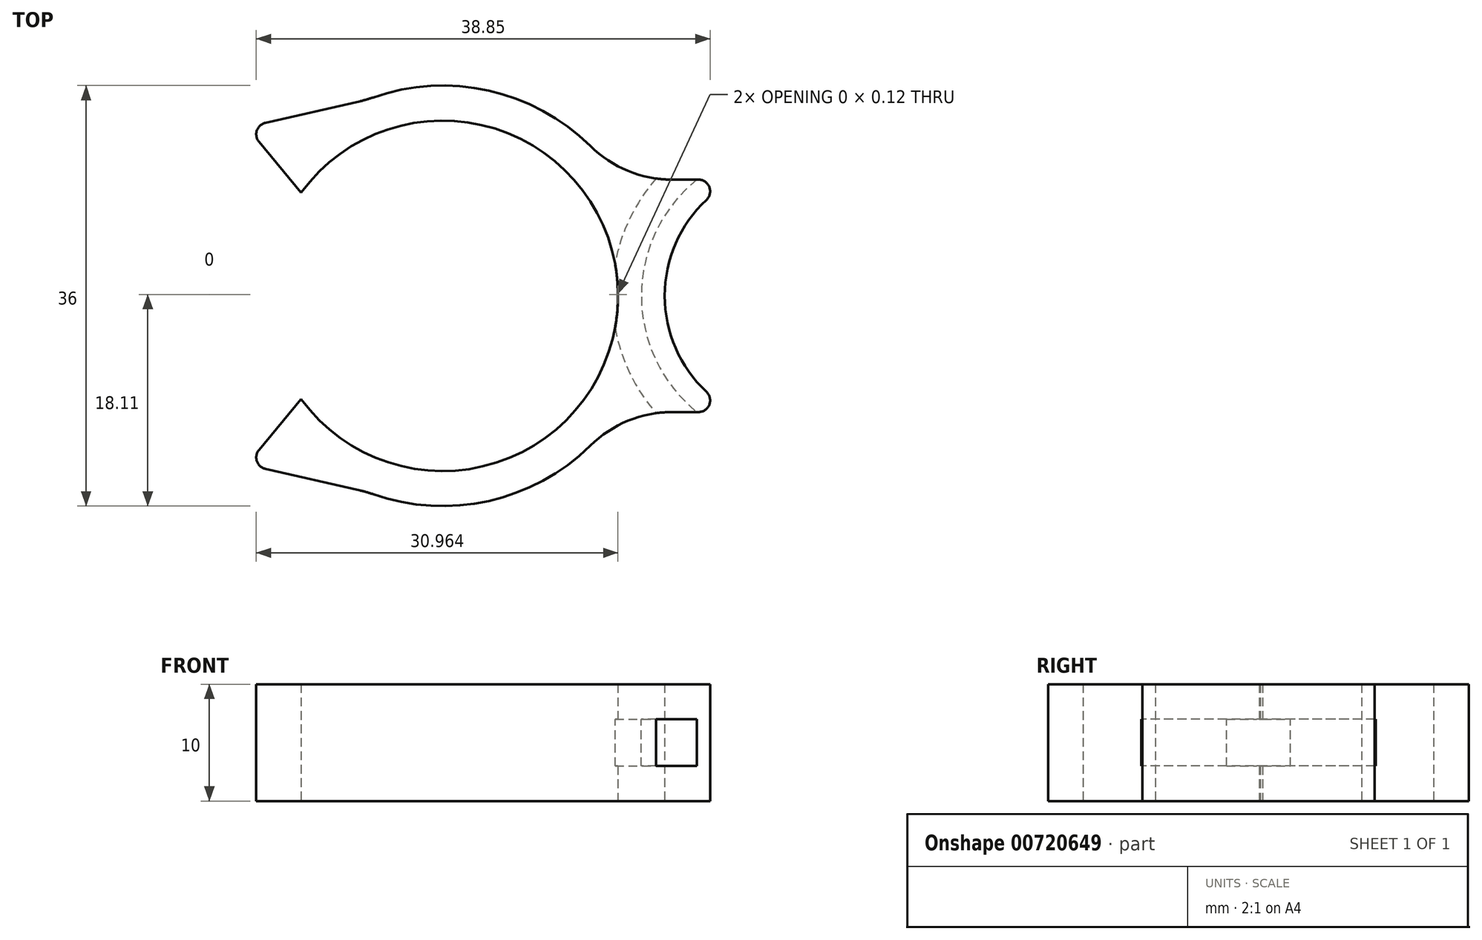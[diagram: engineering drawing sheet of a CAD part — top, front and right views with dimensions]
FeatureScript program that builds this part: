
annotation { "Feature Type Name" : "Feature", "Feature Type Description" : "" }
export const myFeature = defineFeature(function(context is Context, id is Id, definition is map)
    precondition{}
    {
        {
            var Q0;
            Q0=qCreatedBy(makeId("Top.planeOp"),FACE);
            var sketch = newSketch(context, id + "F0", { "sketchPlane" : qUnion([Q0])});
            skArc(sketch, "E0", {"start": v(-28.92, -8.84) * mm, "mid": v(-1.8, 0) * mm, "end": v(-28.92, 8.84) * mm});
            skArc(sketch, "E1", {"start": v(8.2, 9.95) * mm, "mid": v(2.2, 0) * mm, "end": v(8.2, -9.95) * mm});
            skArc(sketch, "E2", {"start": v(-23.25, -16.8) * mm, "mid": v(-11.32, -17.15) * mm, "end": v(-1.8, -9.95) * mm});
            skLineSegment(sketch, "E3", {"start": v(-16.8, 0) * mm, "end": v(13.45, 0) * mm, "construction": true});
            skPoint(sketch, "E4", {"position": v(-1.67, 0) * mm});
            skLineSegment(sketch, "E5.trimOffspring", {"start": v(-1.8, 0.05) * mm, "end": v(-1.8, 0.37) * mm});
            skLineSegment(sketch, "E6.bottom", {"start": v(8.2, 9.95) * mm, "end": v(-1.8, 9.95) * mm});
            skLineSegment(sketch, "E6.top", {"start": v(8.2, -9.95) * mm, "end": v(-1.8, -9.95) * mm});
            skLineSegment(sketch, "E6.right", {"start": v(-1.8, 0.17) * mm, "end": v(-1.8, 0.05) * mm});
            skLineSegment(sketch, "E7.trimOffspring", {"start": v(-1.8, 0.17) * mm, "end": v(-1.8, -0.16) * mm});
            skArc(sketch, "E8.trimOffspring", {"start": v(-1.8, 9.95) * mm, "mid": v(-11.32, 17.15) * mm, "end": v(-23.25, 16.8) * mm});
            skLineSegment(sketch, "E9", {"start": v(-28.92, 8.84) * mm, "end": v(-33.56, 14.45) * mm});
            skLineSegment(sketch, "E10", {"start": v(-33.56, 14.45) * mm, "end": v(-23.25, 16.8) * mm});
            skLineSegment(sketch, "E11.MirrorCS", {"start": v(-28.92, -8.84) * mm, "end": v(-33.56, -14.45) * mm});
            skLineSegment(sketch, "E12.MirrorCS", {"start": v(-33.56, -14.45) * mm, "end": v(-23.25, -16.8) * mm});
            skLineSegment(sketch, "E13", {"start": v(-9.06, 0) * mm, "end": v(-9.06, 9.95) * mm, "construction": true});
            skLineSegment(sketch, "E14", {"start": v(-9.06, 0) * mm, "end": v(-9.06, -9.95) * mm, "construction": true});
            skSolve(sketch);
        }
        {
            var Q0;
            Q0 = qSketchRegion(id + "F0", true);
            extrude(context, id + "F1", {"entities" : qUnion([Q0]), "depth" : 10 * mm, "offsetDistance" : 25 * mm});
        }
        {
            var Q0;
            Q0=makeQuery(id+"F1.opExtrude","SWEPT_EDGE",EDGE,{"disambiguationData":[OSD([sQuery(id+"F0.wireOp",EDGE,"IWztPc0H-4Czz-cEDn-FhKq-w9oCYmKX9AF6"),sQuery(id+"F0.wireOp",EDGE,"92DBHX5X-K6kR-Upr4-bK9H-dtZGLeEnyNnV")])]});
            var Q1;
            Q1=makeQuery(id+"F1.opExtrude","SWEPT_EDGE",EDGE,{"disambiguationData":[OSD([sQuery(id+"F0.wireOp",EDGE,"IWztPc0H-4Czz-cEDn-FhKq-w9oCYmKX9AF6"),sQuery(id+"F0.wireOp",EDGE,"024c119b-de07-41a7-b339-62df15f0e614.trimOffspring")])]});
            var Q2;
            Q2=makeQuery(id+"F1.opExtrude","SWEPT_EDGE",EDGE,{"disambiguationData":[OSD([sQuery(id+"F0.wireOp",EDGE,"3e003569-1aac-4e3d-9f3d-77501b08c2a10.MirrorCS"),sQuery(id+"F0.wireOp",EDGE,"be3c4033-0644-41de-af03-7eb39c3d72080.MirrorCS")])]});
            var Q3;
            Q3=makeQuery(id+"F1.opExtrude","SWEPT_EDGE",EDGE,{"disambiguationData":[OSD([sQuery(id+"F0.wireOp",EDGE,"MHDpRclH-q2Dj-4ouE-9ryf-v0UQ6AgA5fog"),sQuery(id+"F0.wireOp",EDGE,"Bm5BC6q6-ifkZ-6Eal-UUqP-6c5QV21PyJyv")])]});
            var Q4;
            Q4=makeQuery(id+"F1.opExtrude","SWEPT_EDGE",EDGE,{"disambiguationData":[OSD([sQuery(id+"F0.wireOp",EDGE,"E11.MirrorCS"),sQuery(id+"F0.wireOp",EDGE,"E12.MirrorCS")])]});
            var Q5;
            Q5=makeQuery(id+"F1.opExtrude","SWEPT_EDGE",EDGE,{"disambiguationData":[OSD([sQuery(id+"F0.wireOp",EDGE,"E9"),sQuery(id+"F0.wireOp",EDGE,"E10")])]});
            fillet(context, id + "F2", {"entities" : qUnion([Q0, Q1, Q2, Q3, Q4, Q5]), "tangentPropagation" : true, "radius" : 1 * mm, "defaultsChanged" : false, "vertexSettings" : [], "allowEdgeOverflow" : false});
        }
        {
            var Q0;
            Q0=makeQuery(id+"F1.opExtrude","SWEPT_EDGE",EDGE,{"disambiguationData":[OSD([sQuery(id+"F0.wireOp",EDGE,"E6.bottom"),sQuery(id+"F0.wireOp",EDGE,"E8.trimOffspring")])]});
            var Q1;
            Q1=makeQuery(id+"F1.opExtrude","SWEPT_EDGE",EDGE,{"disambiguationData":[OSD([sQuery(id+"F0.wireOp",EDGE,"E2"),sQuery(id+"F0.wireOp",EDGE,"E6.top")])]});
            var Q2;
            Q2=makeQuery(id+"F1.opExtrude","SWEPT_EDGE",EDGE,{"disambiguationData":[OSD([sQuery(id+"F0.wireOp",EDGE,"E8.trimOffspring"),sQuery(id+"F0.wireOp",EDGE,"E10")])]});
            var Q3;
            Q3=makeQuery(id+"F1.opExtrude","SWEPT_EDGE",EDGE,{"disambiguationData":[OSD([sQuery(id+"F0.wireOp",EDGE,"E2"),sQuery(id+"F0.wireOp",EDGE,"E12.MirrorCS")])]});
            fillet(context, id + "F3", {"entities" : qUnion([Q0, Q1, Q2, Q3]), "tangentPropagation" : true, "radius" : 10 * mm, "defaultsChanged" : false, "vertexSettings" : [], "allowEdgeOverflow" : false});
        }
        {
            var Q0;
            Q0=makeQuery(id+"F1.opExtrude","CAP_FACE",FACE,{"disambiguationData":[OSD([sQuery(id+"F0.wireOp",EDGE,"E0"),sQuery(id+"F0.wireOp",EDGE,"E1"),sQuery(id+"F0.wireOp",EDGE,"E2"),sQuery(id+"F0.wireOp",EDGE,"MHDpRclH-q2Dj-4ouE-9ryf-v0UQ6AgA5fog"),sQuery(id+"F0.wireOp",EDGE,"78308c44-5025-46c9-aef0-875acc5395fe.trimOffspring"),sQuery(id+"F0.wireOp",EDGE,"E6.bottom"),sQuery(id+"F0.wireOp",EDGE,"E6.top"),sQuery(id+"F0.wireOp",EDGE,"E8.trimOffspring")])],"isStart":false});
            cPlane(context, id + "F4", {"entities" : qUnion([Q0]), "cplaneType" : CPlaneType.OFFSET, "offset" : 3 * mm, "oppositeDirection" : true, "width" : 150 * mm, "height" : 150 * mm});
        }
        {
            var Q0;
            Q0=qCreatedBy(id+"F4.planeOp",FACE);
            var sketch = newSketch(context, id + "F5", { "sketchPlane" : qUnion([Q0])});
            skArc(sketch, "E15", {"start": v(7.94, 11.74) * mm, "mid": v(0.34, -1.85) * mm, "end": v(11.53, -12.7) * mm});
            skArc(sketch, "E16", {"start": v(3.2, 11.74) * mm, "mid": v(-2.27, -0.8) * mm, "end": v(4.48, -12.7) * mm});
            skLineSegment(sketch, "E17", {"start": v(3.2, 11.74) * mm, "end": v(7.94, 11.74) * mm});
            skLineSegment(sketch, "E18", {"start": v(11.53, -12.7) * mm, "end": v(4.48, -12.7) * mm});
            skSolve(sketch);
        }
        {
            var Q0;
            Q0 = qSketchRegion(id + "F5", true);
            extrude(context, id + "F6", {"entities" : qUnion([Q0]), "operationType" : NewBodyOperationType.REMOVE, "oppositeDirection" : true, "depth" : 4 * mm, "offsetDistance" : 25 * mm});
        }
        {
            var Q0;
            Q0=makeQuery(id+"F1.opExtrude","SWEPT_EDGE",EDGE,{"disambiguationData":[OSD([sQuery(id+"F0.wireOp",EDGE,"E1"),sQuery(id+"F0.wireOp",EDGE,"E6.bottom")])]});
            var Q1;
            Q1=makeQuery(id+"F1.opExtrude","SWEPT_EDGE",EDGE,{"disambiguationData":[OSD([sQuery(id+"F0.wireOp",EDGE,"E1"),sQuery(id+"F0.wireOp",EDGE,"E6.top")])]});
            fillet(context, id + "F7", {"entities" : qUnion([Q0, Q1]), "tangentPropagation" : true, "radius" : 1 * mm, "defaultsChanged" : false, "vertexSettings" : [], "allowEdgeOverflow" : false});
        }
    });
